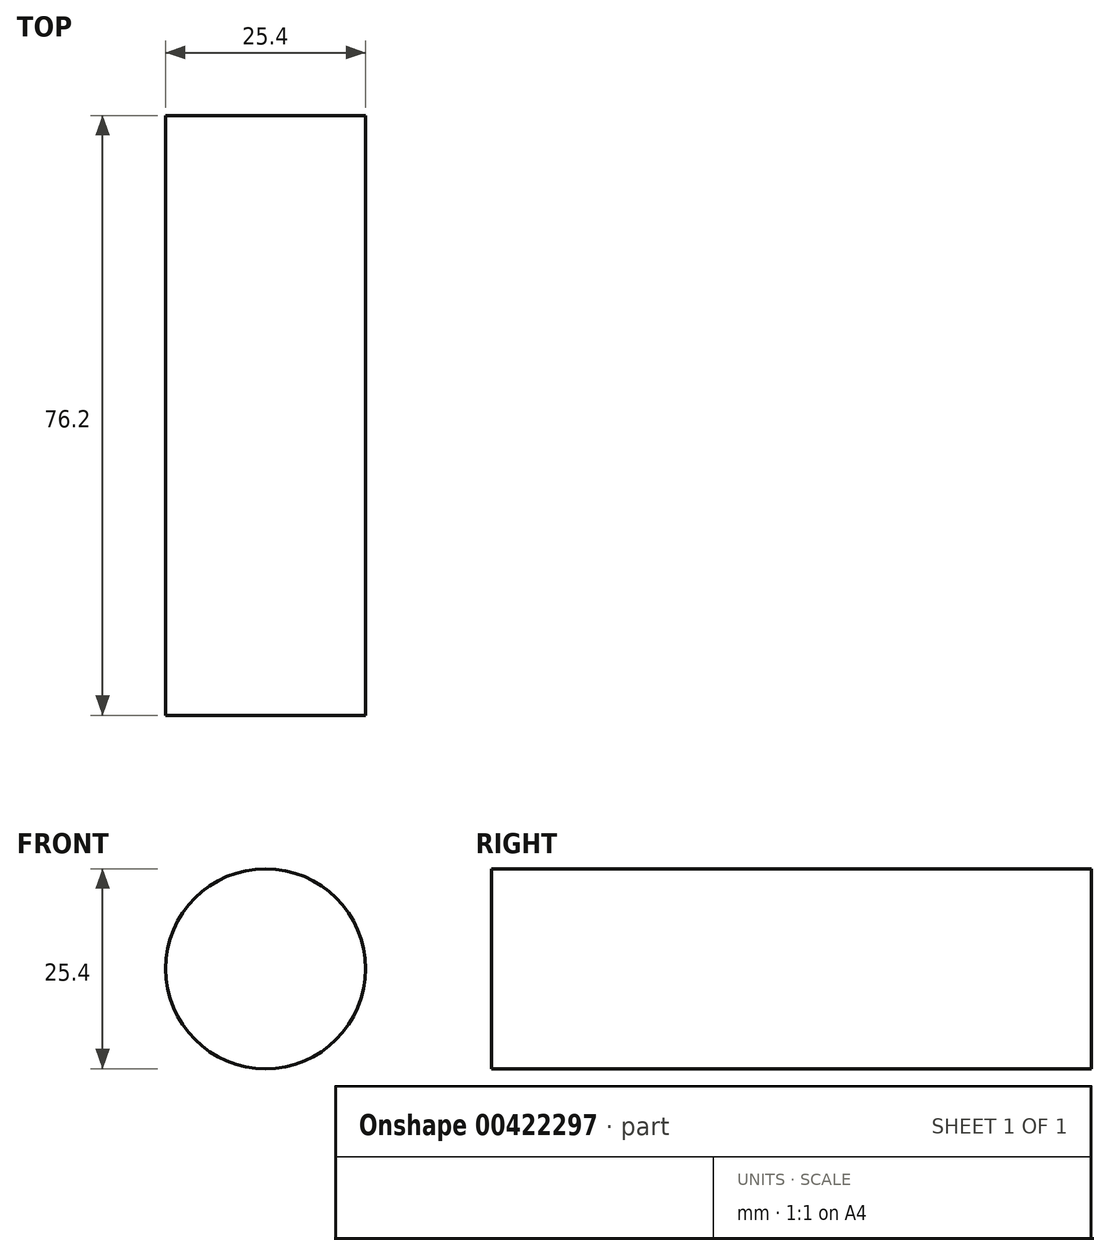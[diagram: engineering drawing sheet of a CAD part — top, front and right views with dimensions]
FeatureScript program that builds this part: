
annotation { "Feature Type Name" : "Feature", "Feature Type Description" : "" }
export const myFeature = defineFeature(function(context is Context, id is Id, definition is map)
    precondition{}
    {
        {
            var Q0;
            Q0=qCreatedBy(makeId("Front.planeOp"),FACE);
            var sketch = newSketch(context, id + "F0", { "sketchPlane" : qUnion([Q0])});
            skCircle(sketch, "E0", {"center": v(-24.86, 10.56) * mm, "radius": 12.7 * mm});
            skSolve(sketch);
        }
        {
            var Q0;
            Q0=makeQuery(id+"F0.imprint","IMPRINT",FACE,{"disambiguationData":[TD([[makeQuery(id+"F0.imprint","IMPRINT",EDGE,{"derivedFrom":sQuery(id+"F0.wireOp",EDGE,"E0")}),1.0]])]});
            extrude(context, id + "F1", {"entities" : qUnion([Q0]), "depth" : 76.2 * mm});
        }
    });
